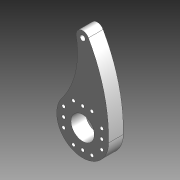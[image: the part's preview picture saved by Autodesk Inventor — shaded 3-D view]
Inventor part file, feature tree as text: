
AUTODESK INVENTOR PART (.ipt)
format: ipt  version: 2014 SP1 (Build 180222100, 222)  size: 194,560 bytes
history: native  units: in
note: dims shown in document units (in); Inventor stores cm internally (conversion verified against a paired STEP export)
features: extrude x4, sketch x4, other x1, move_body x1, imported_body x1
ambient origin geometry x8: Origin, YZ Plane, XZ Plane, XY Plane, X Axis, Y Axis, Z Axis, Center Point
bodies: Solid1 (feature_tree)
feature tree (11):
  other  "Component7.ipt1"
  move_body  "Move Body1"
  extrude  "Extrusion1"  Depth=0.25in
  extrude  "Extrusion2"  Depth=0.1969in TaperAngle=0.0deg
  extrude  "Extrusion3"  Depth=0.1969in TaperAngle=0.0deg
  extrude  "Extrusion4"  [1 undecoded]
  imported_body  "Base1"
  sketch  "Sketch1"  dims[d0=180.0deg d1=0.25in]
  sketch  "Sketch2"  dims[d2=0.4075in d3=0.1969in d4=0.0in]
  sketch  "Sketch3"  dims[d5=0.1969in d6=0.0in d10=0.1969in d11=0.0in]
  sketch  "Sketch4"  dims[d12=0.1969in d13=0.0in]
note: 1 required parameter value undecoded (feature->parameter linkage not recoverable at this tier; creation-order binding heuristic only, values carry confidence <= 0.55)
